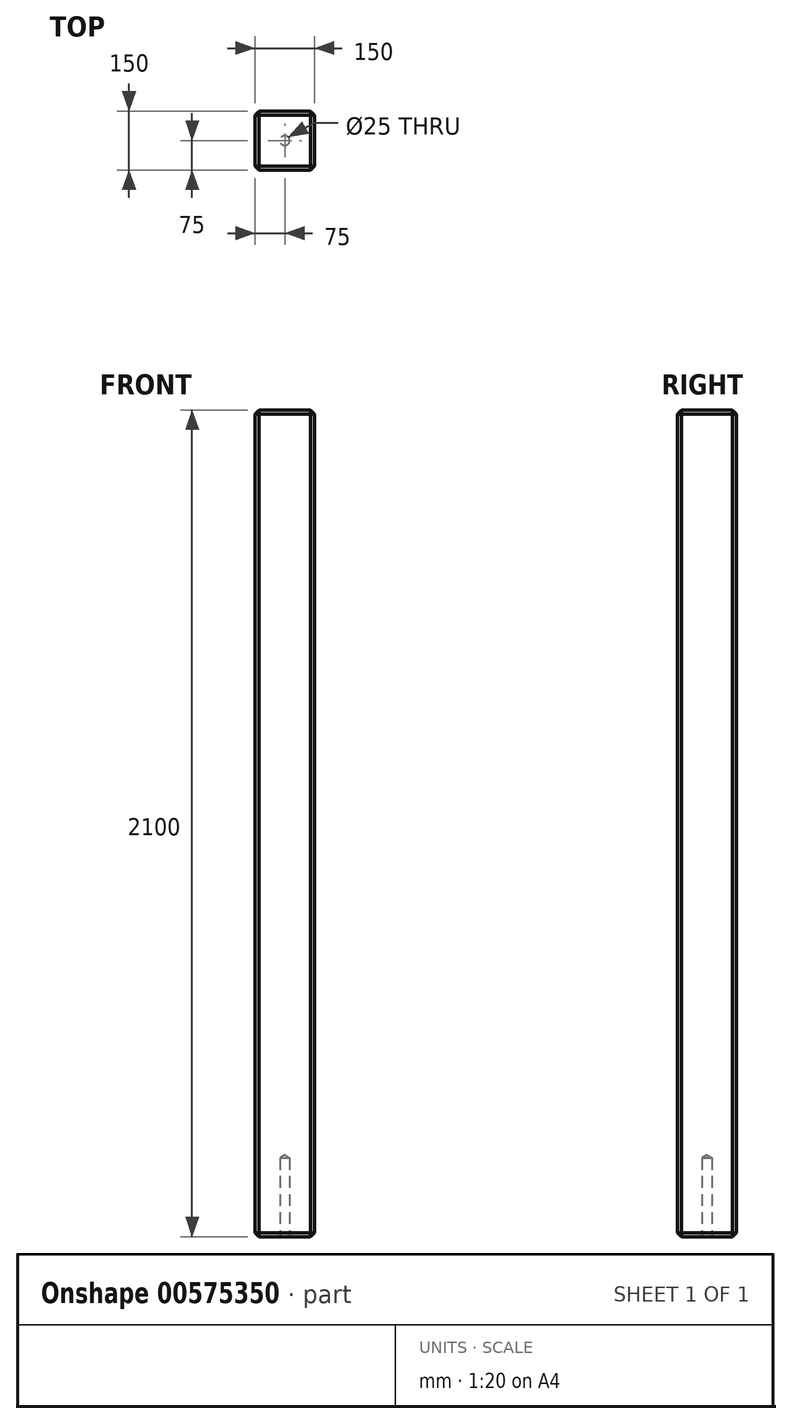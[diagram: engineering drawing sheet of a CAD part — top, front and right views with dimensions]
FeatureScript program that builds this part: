
annotation { "Feature Type Name" : "Feature", "Feature Type Description" : "" }
export const myFeature = defineFeature(function(context is Context, id is Id, definition is map)
    precondition{}
    {
        {
            var Q0;
            Q0=qCreatedBy(makeId("Top.planeOp"),FACE);
            var sketch = newSketch(context, id + "F0", { "sketchPlane" : qUnion([Q0])});
            skLineSegment(sketch, "E0.bottom", {"start": v(-75, 75) * mm, "end": v(75, 75) * mm});
            skLineSegment(sketch, "E0.top", {"start": v(-75, -75) * mm, "end": v(75, -75) * mm});
            skLineSegment(sketch, "E0.left", {"start": v(-75, 75) * mm, "end": v(-75, -75) * mm});
            skLineSegment(sketch, "E0.right", {"start": v(75, 75) * mm, "end": v(75, -75) * mm});
            skPoint(sketch, "E0.middle", {"position": v(0, 0) * mm});
            skSolve(sketch);
        }
        {
            var Q0;
            Q0=makeQuery(id+"F0.imprint","IMPRINT",FACE,{"disambiguationData":[TD([[makeQuery(id+"F0.imprint","IMPRINT",EDGE,{"derivedFrom":sQuery(id+"F0.wireOp",EDGE,"E0.bottom")}),-1.0]])]});
            extrude(context, id + "F1", {"entities" : qUnion([Q0]), "depth" : 2100 * mm, "offsetDistance" : 25 * mm});
        }
        {
            var Q0;
            Q0=makeQuery(id+"F1.opExtrude","CAP_FACE",FACE,{"disambiguationData":[OSD([sQuery(id+"F0.wireOp",EDGE,"E0.bottom"),sQuery(id+"F0.wireOp",EDGE,"E0.top"),sQuery(id+"F0.wireOp",EDGE,"E0.left"),sQuery(id+"F0.wireOp",EDGE,"E0.right")])],"isStart":true});
            var sketch = newSketch(context, id + "F2", { "sketchPlane" : qUnion([Q0])});
            skPoint(sketch, "E1", {"position": v(0, 0) * mm});
            skSolve(sketch);
        }
        {
            var Q0;
            Q0=sQuery(id+"F2.wireOp",VERTEX,"E1");
            var Q1;
            Q1=makeQuery(id+"F1.opExtrude","SWEPT_BODY",BODY,{"disambiguationData":[OSD([sQuery(id+"F0.wireOp",EDGE,"E0.bottom"),sQuery(id+"F0.wireOp",EDGE,"E0.top"),sQuery(id+"F0.wireOp",EDGE,"E0.left"),sQuery(id+"F0.wireOp",EDGE,"E0.right")])]});
            hole(context, id + "F3", {"style" : HoleStyle.SIMPLE, "endStyle" : HoleEndStyle.BLIND, "holeDiameter" : 25 * mm, "holeDepth" : 200 * mm, "startFromSketch" : true, "locations" : qUnion([Q0]), "scope" : qUnion([Q1])});
        }
        {
            var Q0;
            Q0=makeQuery(id+"F1.opExtrude","SWEPT_FACE",FACE,{"disambiguationData":[OSD([sQuery(id+"F0.wireOp",EDGE,"E0.left")])]});
            var Q1;
            Q1=makeQuery(id+"F1.opExtrude","CAP_EDGE",EDGE,{"disambiguationData":[OSD([sQuery(id+"F0.wireOp",EDGE,"E0.bottom")])],"isStart":false});
            var Q2;
            Q2=makeQuery(id+"F1.opExtrude","SWEPT_FACE",FACE,{"disambiguationData":[OSD([sQuery(id+"F0.wireOp",EDGE,"E0.bottom")])]});
            var Q3;
            Q3=makeQuery(id+"F1.opExtrude","SWEPT_FACE",FACE,{"disambiguationData":[OSD([sQuery(id+"F0.wireOp",EDGE,"E0.right")])]});
            var Q4;
            Q4=makeQuery(id+"F1.opExtrude","SWEPT_FACE",FACE,{"disambiguationData":[OSD([sQuery(id+"F0.wireOp",EDGE,"E0.top")])]});
            chamfer(context, id + "F4", {"entities" : qUnion([Q0, Q1, Q2, Q3, Q4]), "width" : 10 * mm, "tangentPropagation" : true});
        }
    });
